# Revit family: Faucet-Kitchen-Grohe-Concetto-31492_Series
name_source: partatom
category: Plumbing Fixtures
revit_build: Autodesk Revit 2018 (Build: 20170223_1515(x64)
units: mm (PartAtom-declared; Revit-internal decimal feet)

## family parameters
Always vertical = No
Cut with Voids When Loaded = No
OmniClass Number = 23.45.55.17
OmniClass Title = Mixing Faucets
Part Type = Normal
Room Calculation Point = No
Round Connector Dimension = Use Diameter
Shared = Yes
Work Plane-Based = Yes

## types (2) — shared parameters
Assembly Code = D2020300
CW Connection = Yes
CWFU = 1.5
CalGreen Compliant = Yes
Cold Water Connection Diameter = 3/8"
Default Elevation = 0"
Description = Single-lever sink mixer 1/2"
Flow Rate = 1.5 gpm (5.7 L/min)
HW Connection = Yes
HWFU = 1.5
Height = 20 1/16"
Hose Colour = Silicone-Grohe-Black
Hot Water Connection Diameter = 0"
Installation Type = Deck-Mounted
Length = 9 1/4"
Manufacturer = Grohe
Price = Prices may vary. Please consult Manufacturer Representative for most up-to-date price list.
Product Page URL = https://www.grohe.com
Shipping Weight = 9.43 lb
URL = http://www.grohe.com
Vent Connection = No
Warranty Documentation Link = https://cdn.cloud.grohe.com
Waste Connection = No
cUPC Compliant = Yes
zero-valued in all types: WFU

## per-type parameters (varying)
| type | Finish | Material |
| 31492000 | Metal-Grohe-000-Chrome | Metal-Grohe-000-Chrome |
| 31492DC0 | Metal-Grohe-DC0-Stainless Steel | Metal-Grohe-DC0-Stainless Steel |

note: column(s) folded — value = type name in every type: Model

## geometry (parser evidence)
native form markers: Sweep x2
no freeform markers — native parametric forms only
